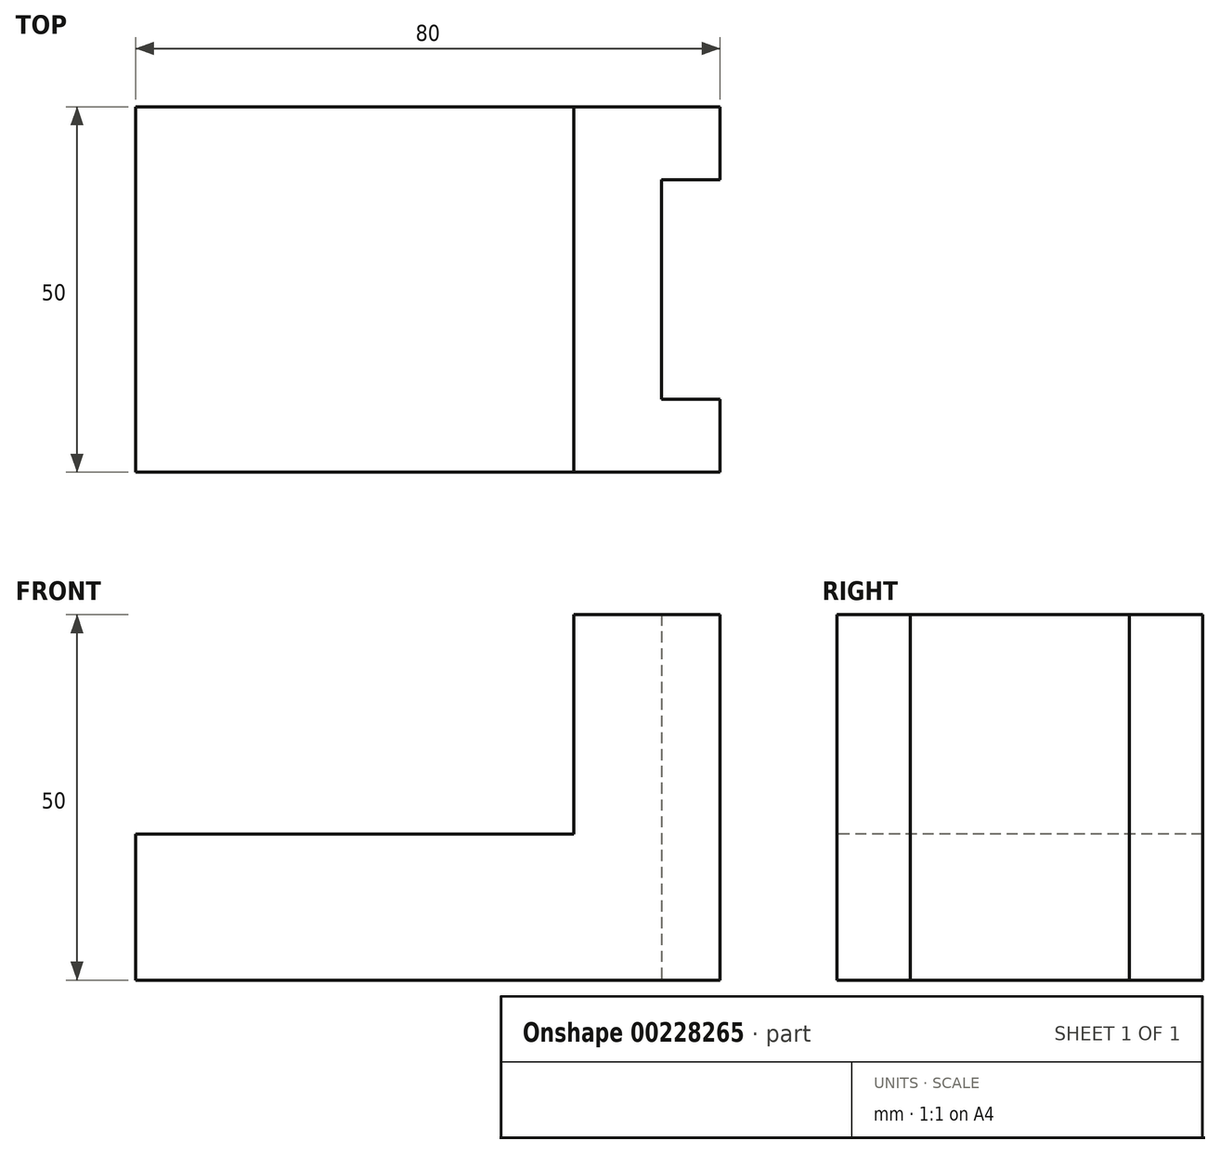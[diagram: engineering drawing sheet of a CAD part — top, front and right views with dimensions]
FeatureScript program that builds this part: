
annotation { "Feature Type Name" : "Feature", "Feature Type Description" : "" }
export const myFeature = defineFeature(function(context is Context, id is Id, definition is map)
    precondition{}
    {
        {
            var Q0;
            Q0=qCreatedBy(makeId("Front.planeOp"),FACE);
            var sketch = newSketch(context, id + "F0", { "sketchPlane" : qUnion([Q0])});
            skLineSegment(sketch, "E0", {"start": v(0, 0) * mm, "end": v(80, 0) * mm});
            skLineSegment(sketch, "E1", {"start": v(80, 0) * mm, "end": v(80, 50) * mm});
            skLineSegment(sketch, "E2", {"start": v(60, 50) * mm, "end": v(60, 20) * mm});
            skLineSegment(sketch, "E3", {"start": v(60, 20) * mm, "end": v(0, 20) * mm});
            skLineSegment(sketch, "E4", {"start": v(0, 20) * mm, "end": v(0, 0) * mm});
            skLineSegment(sketch, "E5", {"start": v(60, 50) * mm, "end": v(80, 50) * mm});
            skSolve(sketch);
        }
        {
            var Q0;
            Q0=makeQuery(id+"F0.imprint","IMPRINT",FACE,{"disambiguationData":[TD([[makeQuery(id+"F0.imprint","IMPRINT",EDGE,{"derivedFrom":sQuery(id+"F0.wireOp",EDGE,"E0")}),1.0]])]});
            extrude(context, id + "F1", {"entities" : qUnion([Q0]), "oppositeDirection" : true, "depth" : 50 * mm});
        }
        {
            var Q0;
            Q0=qCreatedBy(makeId("Top.planeOp"),FACE);
            var sketch = newSketch(context, id + "F2", { "sketchPlane" : qUnion([Q0])});
            skLineSegment(sketch, "E6.0", {"start": v(80, 50) * mm, "end": v(80, 0) * mm, "construction": true});
            skPoint(sketch, "E7.0", {"position": v(70, 50) * mm});
            skLineSegment(sketch, "E8.0", {"start": v(60, 0) * mm, "end": v(80, 0) * mm, "construction": true});
            skLineSegment(sketch, "E9.0", {"start": v(60, 50) * mm, "end": v(80, 50) * mm, "construction": true});
            skLineSegment(sketch, "E10.0.1", {"start": v(80, 0) * mm, "end": v(80, 50) * mm, "construction": true});
            skLineSegment(sketch, "E10.0.2", {"start": v(80, 50) * mm, "end": v(60, 50) * mm, "construction": true});
            skLineSegment(sketch, "E10.0.3", {"start": v(60, 50) * mm, "end": v(60, 0) * mm, "construction": true});
            skLineSegment(sketch, "E11.0", {"start": v(60, 50) * mm, "end": v(0, 50) * mm, "construction": true});
            skLineSegment(sketch, "E12.0.0", {"start": v(0, 0) * mm, "end": v(60, 0) * mm, "construction": true});
            skLineSegment(sketch, "E12.0.1", {"start": v(60, 0) * mm, "end": v(60, 50) * mm, "construction": true});
            skLineSegment(sketch, "E12.0.3", {"start": v(0, 50) * mm, "end": v(0, 0) * mm, "construction": true});
            skLineSegment(sketch, "E13", {"start": v(80, 40) * mm, "end": v(72, 40) * mm});
            skLineSegment(sketch, "E14", {"start": v(72, 40) * mm, "end": v(72, 10) * mm});
            skLineSegment(sketch, "E15", {"start": v(72, 10) * mm, "end": v(80, 10) * mm});
            skLineSegment(sketch, "E16", {"start": v(80, 10) * mm, "end": v(80, 40) * mm});
            skSolve(sketch);
        }
        {
            var Q0;
            Q0=makeQuery(id+"F2.imprint","IMPRINT",FACE,{"disambiguationData":[TD([[makeQuery(id+"F2.imprint","IMPRINT",EDGE,{"derivedFrom":sQuery(id+"F2.wireOp",EDGE,"E13")}),1.0]])]});
            extrude(context, id + "F3", {"entities" : qUnion([Q0]), "operationType" : NewBodyOperationType.REMOVE, "endBound" : BoundingType.THROUGH_ALL, "depth" : 25 * mm});
        }
    });
